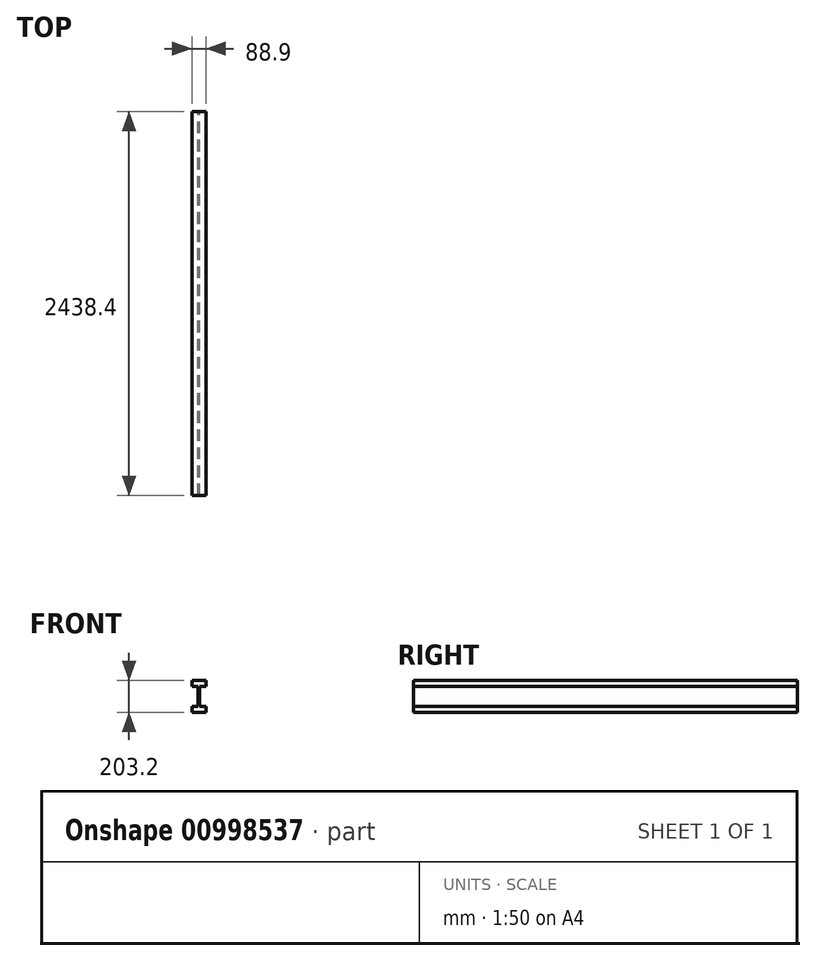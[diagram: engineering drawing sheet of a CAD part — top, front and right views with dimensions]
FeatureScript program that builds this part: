
annotation { "Feature Type Name" : "Feature", "Feature Type Description" : "" }
export const myFeature = defineFeature(function(context is Context, id is Id, definition is map)
    precondition{}
    {
        {
            var Q0;
            Q0=qCreatedBy(makeId("Front.planeOp"),FACE);
            var sketch = newSketch(context, id + "F0", { "sketchPlane" : qUnion([Q0])});
            skLineSegment(sketch, "E0.bottom", {"start": v(-49.53, 142.87) * mm, "end": v(39.37, 142.87) * mm});
            skLineSegment(sketch, "E0.top", {"start": v(-49.53, 104.77) * mm, "end": v(-10.16, 104.77) * mm});
            skLineSegment(sketch, "E0.left", {"start": v(-49.53, 142.87) * mm, "end": v(-49.53, 104.77) * mm});
            skLineSegment(sketch, "E0.right", {"start": v(39.37, 142.87) * mm, "end": v(39.37, 104.77) * mm});
            skLineSegment(sketch, "E1.bottom", {"start": v(-49.53, -22.23) * mm, "end": v(-10.16, -22.23) * mm});
            skLineSegment(sketch, "E1.top", {"start": v(-49.53, -60.33) * mm, "end": v(39.37, -60.33) * mm});
            skLineSegment(sketch, "E1.left", {"start": v(-49.53, -22.23) * mm, "end": v(-49.53, -60.33) * mm});
            skLineSegment(sketch, "E1.right", {"start": v(39.37, -22.23) * mm, "end": v(39.37, -60.33) * mm});
            skLineSegment(sketch, "E2.left", {"start": v(-10.16, 104.77) * mm, "end": v(-10.16, -22.23) * mm});
            skLineSegment(sketch, "E2.right", {"start": v(0, 104.77) * mm, "end": v(0, -22.23) * mm});
            skPoint(sketch, "E3.orphan", {"position": v(0, 123.82) * mm});
            skLineSegment(sketch, "E4.trimOffspring", {"start": v(0, 104.77) * mm, "end": v(39.37, 104.77) * mm});
            skPoint(sketch, "E5.orphan", {"position": v(0, -41.28) * mm});
            skLineSegment(sketch, "E6.trimOffspring", {"start": v(0, -22.23) * mm, "end": v(39.37, -22.23) * mm});
            skSolve(sketch);
        }
        {
            var Q0;
            Q0 = qSketchRegion(id + "F0", true);
            extrude(context, id + "F1", {"entities" : qUnion([Q0]), "depth" : 2438.4 * mm, "offsetDistance" : 25.4 * mm});
        }
    });
